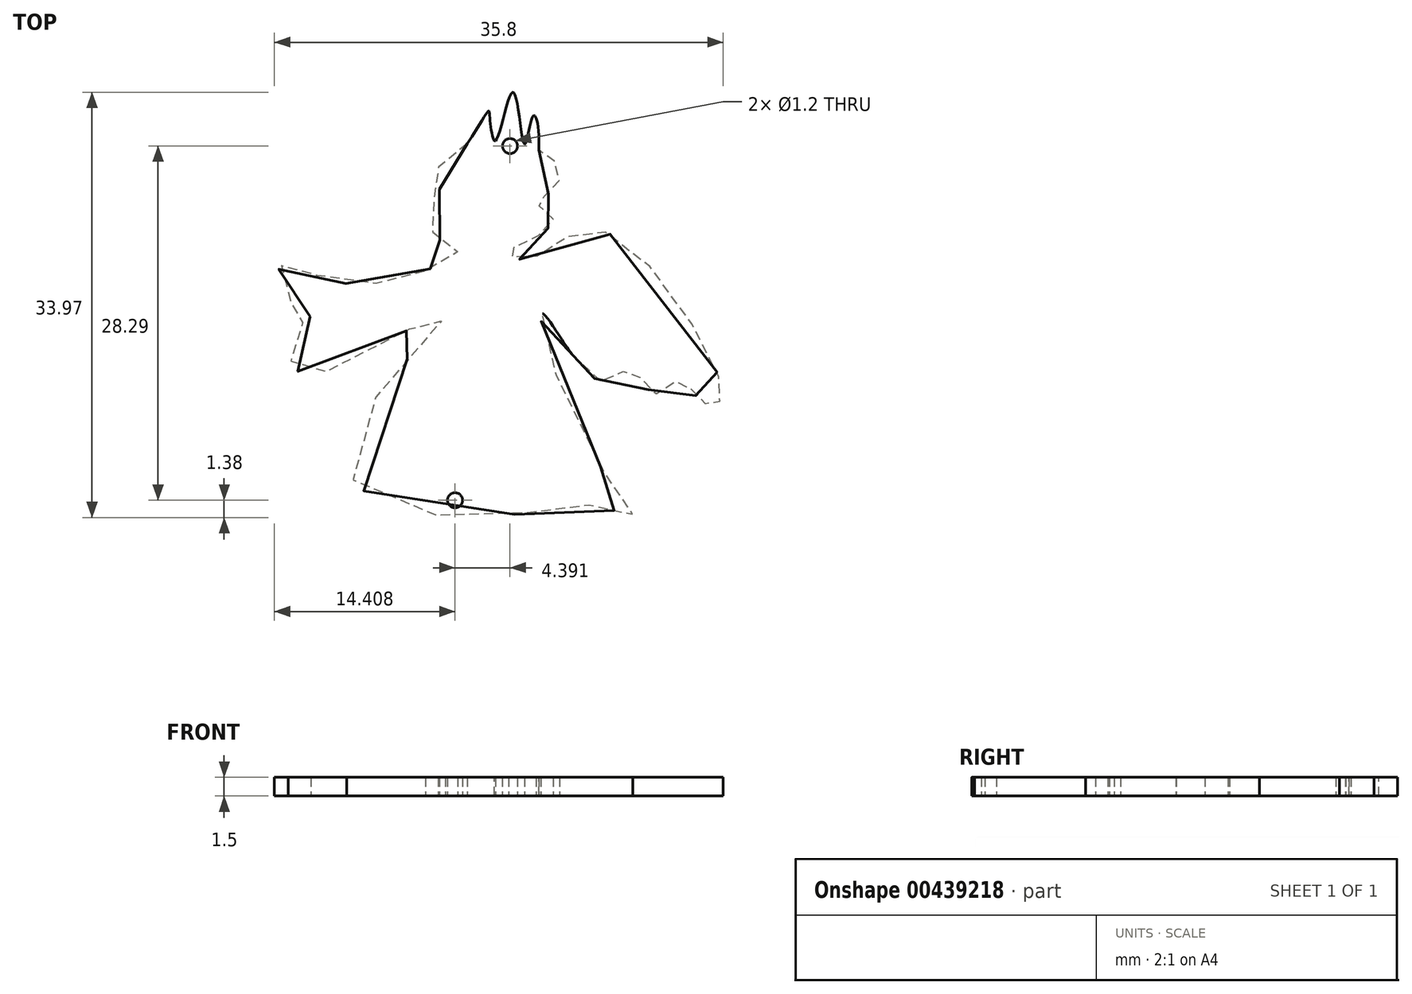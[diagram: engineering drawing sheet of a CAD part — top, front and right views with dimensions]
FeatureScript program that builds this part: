
annotation { "Feature Type Name" : "Feature", "Feature Type Description" : "" }
export const myFeature = defineFeature(function(context is Context, id is Id, definition is map)
    precondition{}
    {
        {
            var Q0;
            Q0=qCreatedBy(makeId("Top.planeOp"),FACE);
            var sketch = newSketch(context, id + "F0", { "sketchPlane" : qUnion([Q0])});
            skFitSpline(sketch, "E0", {"points": [v(-3.53, 0) * mm, v(-11.43, -11.64) * mm, v(0, -16.24) * mm, v(7.87, -15.26) * mm, v(11.38, -16.02) * mm, v(7.76, -10.43) * mm, v(4.25, 0) * mm, v(8.86, -5.39) * mm, v(11.27, -4.4) * mm, v(13.13, -6.37) * mm, v(15.22, -5.28) * mm, v(16.75, -6.92) * mm, v(17.85, -7.14) * mm, v(18.62, -6.48) * mm, v(9.08, 6.56) * mm, v(3.15, 4.37) * mm, v(1.51, 4.92) * mm, v(3.48, 6.02) * mm, v(5.02, 7.77) * mm, v(3.7, 8.87) * mm, v(5.12, 9.88) * mm, v(5.35, 11.93) * mm, v(3.91, 13.07) * mm, v(2.77, 13.55) * mm, v(0.47, 13.83) * mm, v(-2.43, 13.37) * mm, v(-4.08, 11.71) * mm, v(-4.08, 9.64) * mm, v(-5.07, 8.43) * mm, v(-3.86, 5.8) * mm, v(-2.54, 5.03) * mm, v(-4.08, 3.93) * mm, v(-7.26, 2.73) * mm, v(-13.3, 2.84) * mm, v(-16.15, 4.15) * mm, v(-17.02, 1.85) * mm, v(-14.28, 0) * mm, v(-15.7, -1.44) * mm, v(-15.6, -4.3) * mm, v(-12.53, -4.4) * mm, v(-3.53, 0) * mm]});
            skFitSpline(sketch, "E1", {"points": [v(-1.8, 13.59) * mm, v(0, 15.8) * mm, v(0.47, 13.83) * mm, v(1.86, 17.7) * mm, v(2.77, 13.55) * mm, v(3.45, 15.76) * mm, v(3.91, 13.07) * mm], "startDerivative": vector(33.22, 50.27) * mm, "endDerivative": vector(-1.65, -32.85) * mm});
            skCircle(sketch, "E2", {"center": v(-2.77, -14.89) * mm, "radius": 0.6 * mm});
            skCircle(sketch, "E3", {"center": v(-2.77, -14.89) * mm, "radius": 0.3 * mm});
            skCircle(sketch, "E4", {"center": v(1.62, 13.4) * mm, "radius": 0.3 * mm});
            skCircle(sketch, "E5", {"center": v(1.62, 13.4) * mm, "radius": 0.6 * mm});
            skSolve(sketch);
        }
        {
            var Q0;
            Q0 = qSketchRegion(id + "F0", true);
            extrude(context, id + "F1", {"entities" : qUnion([Q0]), "depth" : 1.5 * mm});
        }
    });
